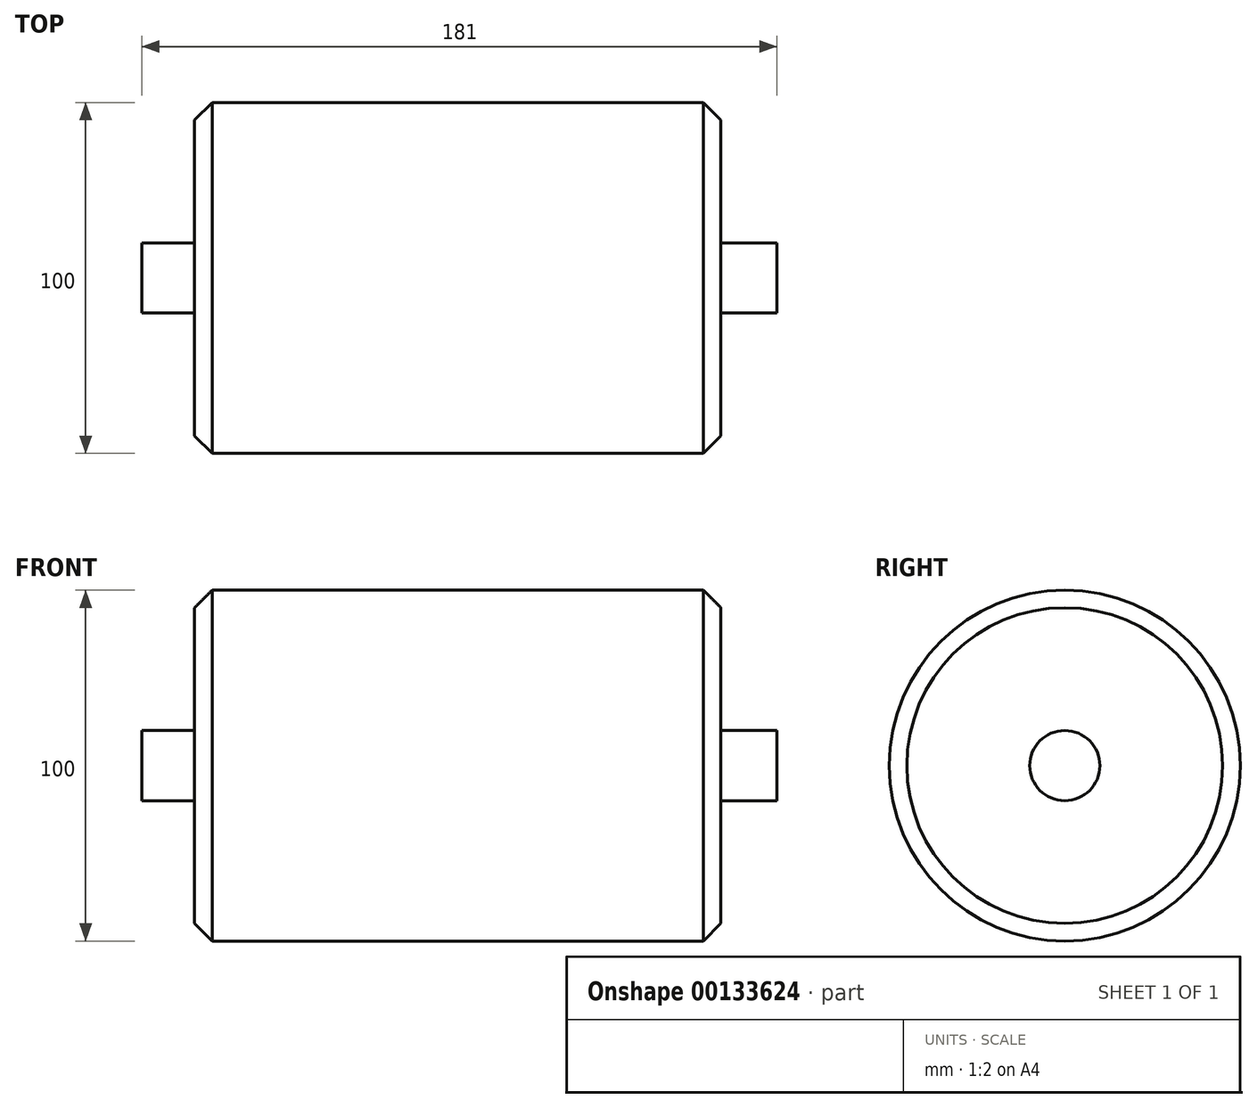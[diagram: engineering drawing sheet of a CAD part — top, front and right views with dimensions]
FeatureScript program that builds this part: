
annotation { "Feature Type Name" : "Feature", "Feature Type Description" : "" }
export const myFeature = defineFeature(function(context is Context, id is Id, definition is map)
    precondition{}
    {
        {
            var Q0;
            Q0=qCreatedBy(makeId("Front.planeOp"),FACE);
            var sketch = newSketch(context, id + "F0", { "sketchPlane" : qUnion([Q0])});
            skLineSegment(sketch, "E0.bottom", {"start": v(0, 0) * mm, "end": v(150, 0) * mm});
            skLineSegment(sketch, "E0.top", {"start": v(0, 50) * mm, "end": v(150, 50) * mm});
            skLineSegment(sketch, "E0.left", {"start": v(0, 0) * mm, "end": v(0, 50) * mm});
            skLineSegment(sketch, "E0.right", {"start": v(150, 0) * mm, "end": v(150, 50) * mm});
            skSolve(sketch);
        }
        {
            var Q0;
            Q0 = qSketchRegion(id + "F0", true);
            var Q1;
            Q1=sQuery(id+"F0.wireOp",EDGE,"E0.bottom");
            revolve(context, id + "F1", {"entities" : qUnion([Q0]), "axis" : qUnion([Q1]), "revolveType" : RevolveType.FULL});
        }
        {
            var Q0;
            Q0=makeQuery(id+"F1.opRevolve","SWEPT_FACE",FACE,{"disambiguationData":[OSD([sQuery(id+"F0.wireOp",EDGE,"E0.left")])]});
            var sketch = newSketch(context, id + "F2", { "sketchPlane" : qUnion([Q0])});
            skCircle(sketch, "E1", {"center": v(0, 0) * mm, "radius": 10 * mm});
            skSolve(sketch);
        }
        {
            var Q0;
            Q0 = qSketchRegion(id + "F2", true);
            extrude(context, id + "F3", {"entities" : qUnion([Q0]), "operationType" : NewBodyOperationType.ADD, "depth" : 15 * mm, "offsetDistance" : 25 * mm});
        }
        {
            var Q0;
            Q0=makeQuery(id+"F1.opRevolve","SWEPT_FACE",FACE,{"disambiguationData":[OSD([sQuery(id+"F0.wireOp",EDGE,"E0.right")])]});
            var sketch = newSketch(context, id + "F4", { "sketchPlane" : qUnion([Q0])});
            skCircle(sketch, "E2", {"center": v(0, 0) * mm, "radius": 10 * mm});
            skSolve(sketch);
        }
        {
            var Q0;
            Q0 = qSketchRegion(id + "F4", true);
            extrude(context, id + "F5", {"entities" : qUnion([Q0]), "operationType" : NewBodyOperationType.ADD, "depth" : 16 * mm, "offsetDistance" : 25 * mm});
        }
        {
            var Q0;
            Q0=makeQuery(id+"F1.opRevolve","SWEPT_EDGE",EDGE,{"disambiguationData":[OSD([sQuery(id+"F0.wireOp",EDGE,"E0.top"),sQuery(id+"F0.wireOp",EDGE,"E0.right")])]});
            chamfer(context, id + "F6", {"entities" : qUnion([Q0]), "chamferType" : ChamferType.OFFSET_ANGLE, "width" : 5 * mm, "oppositeDirection" : false, "angle" : 45 * degree, "tangentPropagation" : true});
        }
        {
            var Q0;
            Q0=makeQuery(id+"F1.opRevolve","SWEPT_EDGE",EDGE,{"disambiguationData":[OSD([sQuery(id+"F0.wireOp",EDGE,"E0.top"),sQuery(id+"F0.wireOp",EDGE,"E0.left")])]});
            chamfer(context, id + "F7", {"entities" : qUnion([Q0]), "chamferType" : ChamferType.OFFSET_ANGLE, "width" : 5 * mm, "oppositeDirection" : false, "angle" : 45 * degree, "tangentPropagation" : true});
        }
    });
